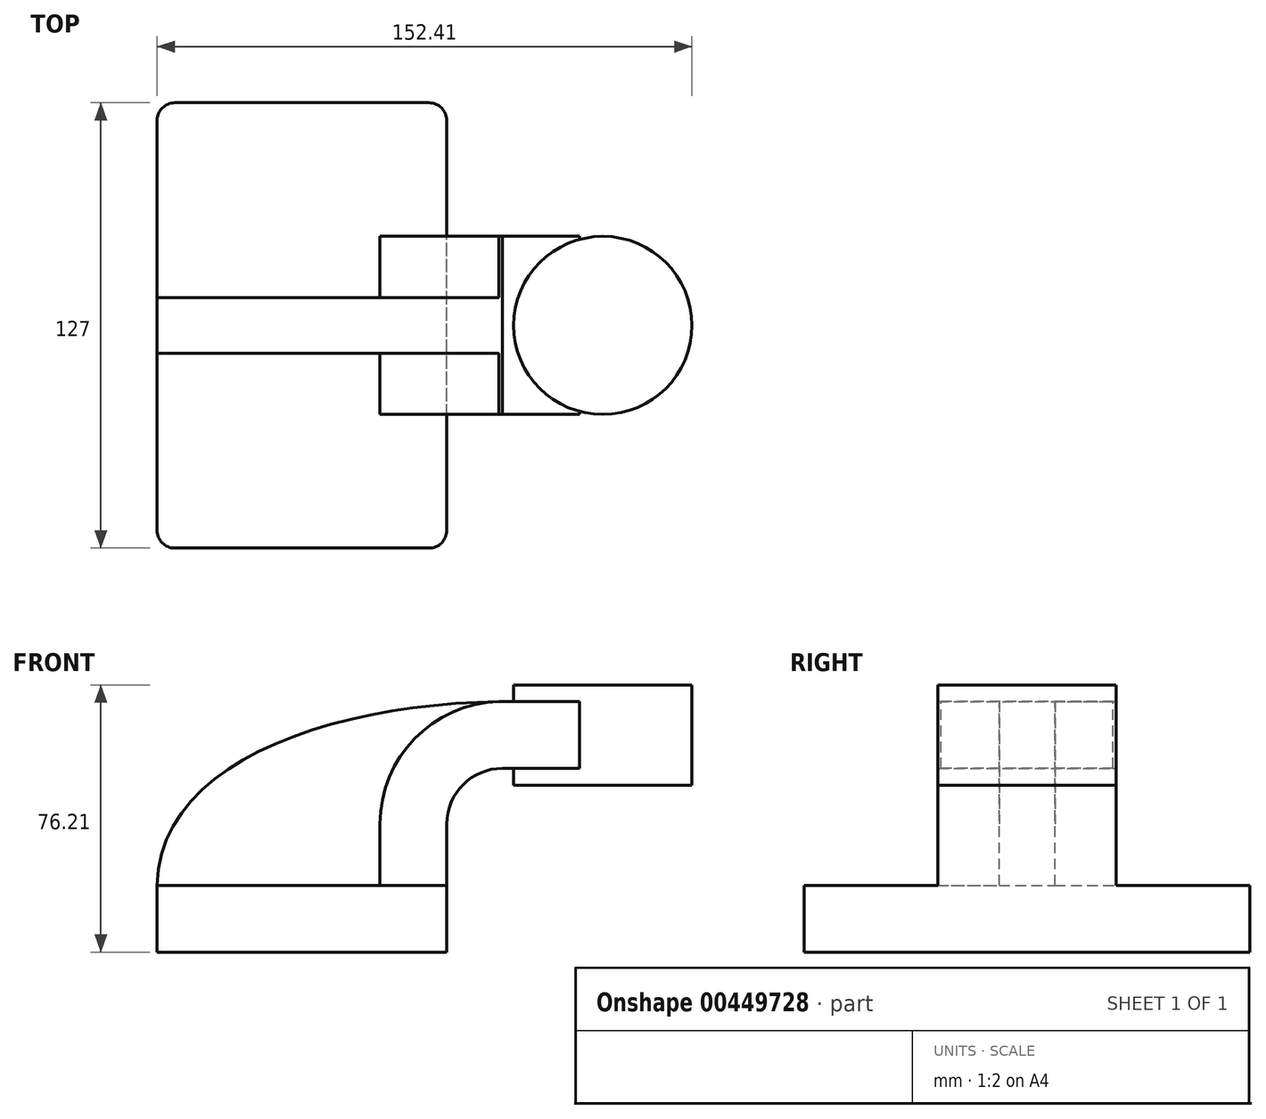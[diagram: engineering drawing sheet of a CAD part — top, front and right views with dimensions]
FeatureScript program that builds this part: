
annotation { "Feature Type Name" : "Feature", "Feature Type Description" : "" }
export const myFeature = defineFeature(function(context is Context, id is Id, definition is map)
    precondition{}
    {
        {
            var Q0;
            Q0=qCreatedBy(makeId("Front.planeOp"),FACE);
            var sketch = newSketch(context, id + "F0", { "sketchPlane" : qUnion([Q0])});
            skLineSegment(sketch, "E0.bottom", {"start": v(-41.27, -9.53) * mm, "end": v(41.28, -9.53) * mm});
            skLineSegment(sketch, "E0.top", {"start": v(-41.28, 9.52) * mm, "end": v(41.28, 9.52) * mm});
            skLineSegment(sketch, "E0.left", {"start": v(-41.28, -9.53) * mm, "end": v(-41.28, 9.52) * mm});
            skLineSegment(sketch, "E0.right", {"start": v(41.28, -9.53) * mm, "end": v(41.28, 9.52) * mm});
            skPoint(sketch, "E0.middle", {"position": v(0, 0) * mm});
            skLineSegment(sketch, "E1.bottom", {"start": v(60.33, 38.1) * mm, "end": v(111.12, 38.1) * mm});
            skLineSegment(sketch, "E1.top", {"start": v(60.32, 66.67) * mm, "end": v(111.12, 66.67) * mm});
            skLineSegment(sketch, "E1.left", {"start": v(60.33, 38.1) * mm, "end": v(60.32, 66.68) * mm});
            skLineSegment(sketch, "E1.right", {"start": v(111.12, 38.1) * mm, "end": v(111.12, 66.68) * mm});
            skPoint(sketch, "E1.middle", {"position": v(85.72, 52.39) * mm});
            skLineSegment(sketch, "E2", {"start": v(41.27, 9.52) * mm, "end": v(41.27, 27) * mm});
            skArc(sketch, "E3", {"start": v(41.27, 27) * mm, "mid": v(45.92, 38.23) * mm, "end": v(57.15, 42.88) * mm});
            skLineSegment(sketch, "E4", {"start": v(57.15, 42.88) * mm, "end": v(79.03, 42.88) * mm});
            skLineSegment(sketch, "E5.0", {"start": v(57.15, 61.93) * mm, "end": v(79.03, 61.93) * mm});
            skArc(sketch, "E5.1", {"start": v(22.22, 27) * mm, "mid": v(32.45, 51.7) * mm, "end": v(57.15, 61.93) * mm});
            skLineSegment(sketch, "E5.2", {"start": v(22.22, 9.52) * mm, "end": v(22.22, 27) * mm});
            skLineSegment(sketch, "E6", {"start": v(79.03, 42.88) * mm, "end": v(79.03, 61.93) * mm});
            skFitSpline(sketch, "E7", {"points": [v(-41.27, 9.53) * mm, v(57.15, 61.93) * mm], "startDerivative": vector(2.45, 107.88) * mm, "endDerivative": vector(142.29, 1.76) * mm});
            skLineSegment(sketch, "E8", {"start": v(85.72, 66.67) * mm, "end": v(85.72, 38.1) * mm});
            skSolve(sketch);
        }
        {
            var Q0;
            Q0=makeQuery(id+"F0.imprint","IMPRINT",FACE,{"disambiguationData":[TD([[makeQuery(id+"F0.imprint","IMPRINT",EDGE,{"derivedFrom":sQuery(id+"F0.wireOp",EDGE,"E0.bottom")}),1.0]])]});
            extrude(context, id + "F1", {"entities" : qUnion([Q0]), "endBound" : BoundingType.SYMMETRIC, "depth" : 127 * mm});
        }
        {
            var Q0;
            {var subQ0=sQuery(id+"F0.wireOp",EDGE,"E2");Q0=makeQuery(id+"F0.imprint","IMPRINT",FACE,{"disambiguationData":[TD([[makeQuery(id+"F0.imprint","IMPRINT",EDGE,{"derivedFrom":subQ0}),1.0]])]});}
            var Q1;
            {var subQ5=sQuery(id+"F0.wireOp",EDGE,"E6");Q1=makeQuery(id+"F0.imprint","IMPRINT",FACE,{"disambiguationData":[TD([[makeQuery(id+"F0.imprint","IMPRINT",EDGE,{"derivedFrom":subQ5}),1.0]])]});}
            extrude(context, id + "F2", {"entities" : qUnion([Q0, Q1]), "operationType" : NewBodyOperationType.ADD, "endBound" : BoundingType.SYMMETRIC, "depth" : 50.8 * mm});
        }
        {
            var Q0;
            {var subQ3=sQuery(id+"F0.wireOp",EDGE,"E5.2");Q0=makeQuery(id+"F0.imprint","IMPRINT",FACE,{"disambiguationData":[TD([[makeQuery(id+"F0.imprint","IMPRINT",EDGE,{"derivedFrom":subQ3}),1.0]])]});}
            extrude(context, id + "F3", {"entities" : qUnion([Q0]), "operationType" : NewBodyOperationType.ADD, "endBound" : BoundingType.SYMMETRIC, "depth" : 15.88 * mm});
        }
        {
            var Q0;
            {var subQ0=sQuery(id+"F0.wireOp",EDGE,"E1.right");Q0=makeQuery(id+"F0.imprint","IMPRINT",FACE,{"disambiguationData":[TD([[makeQuery(id+"F0.imprint","IMPRINT",EDGE,{"derivedFrom":subQ0}),1.0]])]});}
            var Q1;
            Q1=sQuery(id+"F0.wireOp",EDGE,"E8");
            revolve(context, id + "F4", {"operationType" : NewBodyOperationType.ADD, "entities" : qUnion([Q0]), "axis" : qUnion([Q1]), "revolveType" : RevolveType.FULL});
        }
        {
            var Q0;
            Q0=makeQuery(id+"F1.opExtrude","CAP_EDGE",EDGE,{"disambiguationData":[OSD([sQuery(id+"F0.wireOp",EDGE,"E0.right")])],"isStart":false});
            var Q1;
            Q1=makeQuery(id+"F1.opExtrude","CAP_EDGE",EDGE,{"disambiguationData":[OSD([sQuery(id+"F0.wireOp",EDGE,"E0.left")])],"isStart":false});
            var Q2;
            Q2=makeQuery(id+"F1.opExtrude","CAP_EDGE",EDGE,{"disambiguationData":[OSD([sQuery(id+"F0.wireOp",EDGE,"E0.right")])],"isStart":true});
            var Q3;
            Q3=makeQuery(id+"F1.opExtrude","CAP_EDGE",EDGE,{"disambiguationData":[OSD([sQuery(id+"F0.wireOp",EDGE,"E0.left")])],"isStart":true});
            fillet(context, id + "F5", {"entities" : qUnion([Q0, Q1, Q2, Q3]), "radius" : 5.08 * mm, "tangentPropagation" : true, "allowEdgeOverflow" : false});
        }
    });
